# Revit family: Thorn AXYL ETCH M
name_source: partatom
category: Lighting Fixtures
units: mm (PartAtom-declared; Revit-internal decimal feet)

## family parameters
Cut with Voids When Loaded = Yes
Host = Face
Light Source = Yes
Maintain Annotation Orientation = No
Part Type = Normal
Room Calculation Point = Yes
Round Connector Dimension = Use Diameter
Shared = No

## types (1)
- Thorn AXYL ETCH M
    Apparent Load = 8 VA
    Assembly Code = Pr_70_70_48_93
    Color Filter = 16777215
    Default Elevation = 1000 mm  [stored 3.28084 ft]
    Description = Wall Mounted Luminaire
    Dimming Lamp Color Temperature Shift = <None>
    Export Type to IFC As = IfcLightFixtureType
    Lamp = LED
    Luminaire Height = 88 mm  [stored 0.288714 ft]
    Luminaire Length = 41 mm  [stored 0.134514 ft]
    Luminaire Width = 150 mm
    Manufacturer = Thorn Lighting
    Material Housing = Thorn-Aluminium-RAL 7016-Anthracite Grey
    Model = 96700576
    Photometric Web File = 96700576_(STD).IES
    Power Factor = 0.6
    Tilt Angle = 90.00°
    Type IFC Predefined Type = DIRECTIONSOURCE
    Type Image = TLG_AXYL_F_ETCH_ANT.jpg
    URL = https://www.thornlighting.com

note: [stored X ft] marks values corroborated as IEEE doubles in the binary element streams (Revit-internal decimal feet)

## geometry (parser evidence)
native form markers: Sweep x3
no freeform markers — native parametric forms only
